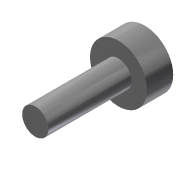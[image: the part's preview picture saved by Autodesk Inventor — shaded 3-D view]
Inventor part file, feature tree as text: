
AUTODESK INVENTOR PART (.ipt)
format: ipt  version: 2014 (Build 180170000, 170)  size: 86,528 bytes
history: native  units: mm
features: revolve x1, sketch x1
ambient origin geometry x8: Origin, YZ Plane, XZ Plane, XY Plane, X Axis, Y Axis, Z Axis, Center Point
bodies: Solid1 (feature_tree)
feature tree (2):
  revolve  "Revolution1"  [1 undecoded]
  sketch  "Sketch1"  dims[d0=6.5mm d1=3.0mm d2=6.0mm d3=19.0mm d4=90.0deg]
note: 1 required parameter value undecoded (feature->parameter linkage not recoverable at this tier; creation-order binding heuristic only, values carry confidence <= 0.55)
